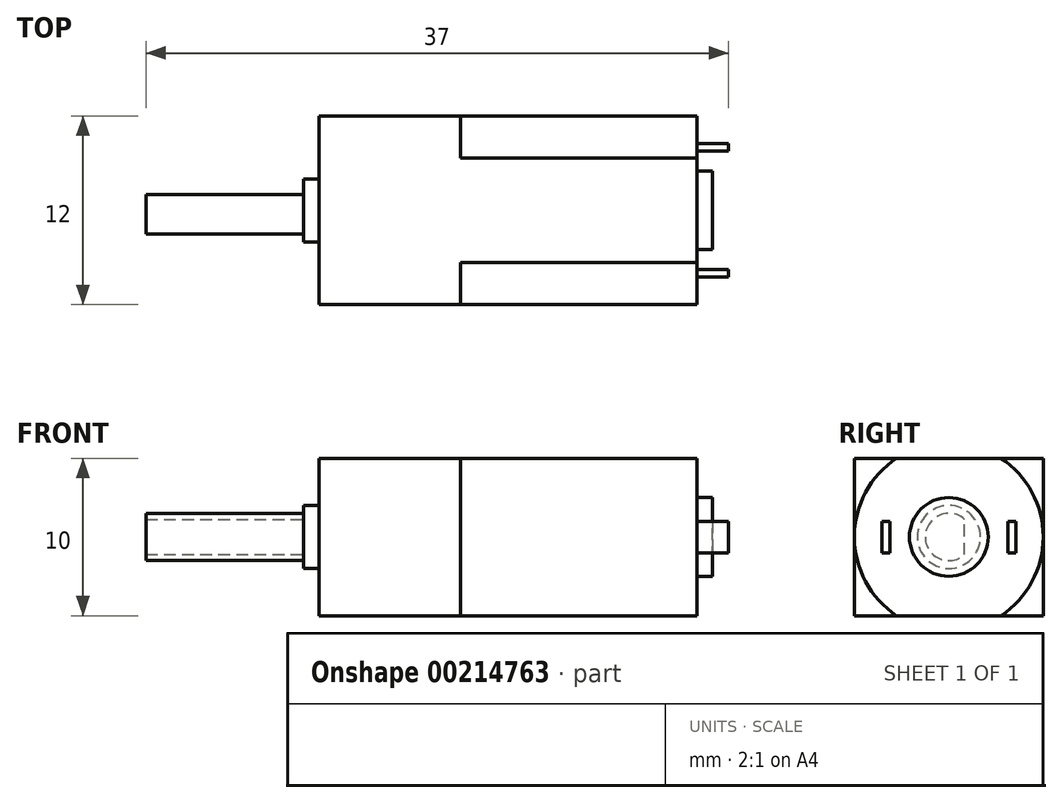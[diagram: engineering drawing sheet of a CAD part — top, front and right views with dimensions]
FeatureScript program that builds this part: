
annotation { "Feature Type Name" : "Feature", "Feature Type Description" : "" }
export const myFeature = defineFeature(function(context is Context, id is Id, definition is map)
    precondition{}
    {
        {
            var Q0;
            Q0=qCreatedBy(makeId("Right.planeOp"),FACE);
            var sketch = newSketch(context, id + "F0", { "sketchPlane" : qUnion([Q0])});
            skLineSegment(sketch, "E0.bottom", {"start": v(6, -5) * mm, "end": v(-6, -5) * mm});
            skLineSegment(sketch, "E0.top", {"start": v(6, 5) * mm, "end": v(-6, 5) * mm});
            skLineSegment(sketch, "E0.left", {"start": v(6, -5) * mm, "end": v(6, 5) * mm});
            skLineSegment(sketch, "E0.right", {"start": v(-6, -5) * mm, "end": v(-6, 5) * mm});
            skPoint(sketch, "E0.middle", {"position": v(0, 0) * mm});
            skCircle(sketch, "E1", {"center": v(0, 0) * mm, "radius": 2 * mm});
            skSolve(sketch);
        }
        {
            var Q0;
            Q0=makeQuery(id+"F0.imprint","IMPRINT",FACE,{"disambiguationData":[TD([[makeQuery(id+"F0.imprint","IMPRINT",EDGE,{"derivedFrom":sQuery(id+"F0.wireOp",EDGE,"E0.bottom")}),-1.0]])]});
            var Q1;
            Q1=makeQuery(id+"F0.imprint","IMPRINT",FACE,{"disambiguationData":[TD([[makeQuery(id+"F0.imprint","IMPRINT",EDGE,{"derivedFrom":sQuery(id+"F0.wireOp",EDGE,"E1")}),1.0]])]});
            extrude(context, id + "F1", {"entities" : qUnion([Q0, Q1]), "depth" : 9 * mm});
        }
        {
            var Q0;
            Q0=makeQuery(id+"F0.imprint","IMPRINT",FACE,{"disambiguationData":[TD([[makeQuery(id+"F0.imprint","IMPRINT",EDGE,{"derivedFrom":sQuery(id+"F0.wireOp",EDGE,"E1")}),1.0]])]});
            extrude(context, id + "F2", {"entities" : qUnion([Q0]), "operationType" : NewBodyOperationType.ADD, "oppositeDirection" : true, "depth" : 1 * mm});
        }
        {
            var Q0;
            Q0=makeQuery(id+"F2.opExtrude","CAP_FACE",FACE,{"disambiguationData":[OSD([sQuery(id+"F0.wireOp",EDGE,"E1")])],"isStart":false});
            var sketch = newSketch(context, id + "F3", { "sketchPlane" : qUnion([Q0])});
            skCircle(sketch, "E2", {"center": v(0, 0) * mm, "radius": 1.5 * mm});
            skLineSegment(sketch, "E3", {"start": v(-1, -1.12) * mm, "end": v(-1, 1.12) * mm});
            skSolve(sketch);
        }
        {
            var Q0;
            {var subQ0=sQuery(id+"F3.wireOp",EDGE,"E3");Q0=makeQuery(id+"F3.imprint","IMPRINT",FACE,{"disambiguationData":[TD([[makeQuery(id+"F3.imprint","IMPRINT",EDGE,{"derivedFrom":subQ0}),-1.0]])]});}
            extrude(context, id + "F4", {"entities" : qUnion([Q0]), "operationType" : NewBodyOperationType.ADD, "depth" : 10 * mm});
        }
        {
            var Q0;
            Q0=makeQuery(id+"F1.opExtrude","CAP_FACE",FACE,{"disambiguationData":[OSD([sQuery(id+"F0.wireOp",EDGE,"E0.bottom"),sQuery(id+"F0.wireOp",EDGE,"E0.top"),sQuery(id+"F0.wireOp",EDGE,"E0.left"),sQuery(id+"F0.wireOp",EDGE,"E0.right")])],"isStart":false});
            var sketch = newSketch(context, id + "F5", { "sketchPlane" : qUnion([Q0])});
            skArc(sketch, "E4", {"start": v(-3.32, 5) * mm, "mid": v(-6, 0) * mm, "end": v(-3.32, -5) * mm});
            skLineSegment(sketch, "E5.0", {"start": v(6, 5) * mm, "end": v(-6, 5) * mm});
            skLineSegment(sketch, "E6.0", {"start": v(6, -5) * mm, "end": v(-6, -5) * mm});
            skArc(sketch, "E7.trimOffspring", {"start": v(3.32, -5) * mm, "mid": v(6, 0) * mm, "end": v(3.32, 5) * mm});
            skSolve(sketch);
        }
        {
            var Q0;
            {var subQ1=sQuery(id+"F5.wireOp",EDGE,"E4");var subQ5=sQuery(id+"F5.wireOp",EDGE,"E5.0");var subQ6=makeQuery(id+"F5.imprint","INTERSECT",VERTEX,{"derivedFrom":[subQ1,subQ5]});Q0=makeQuery(id+"F5.imprint","IMPRINT",FACE,{"disambiguationData":[TD([[makeQuery(id+"F5.imprint","IMPRINT",EDGE,{"disambiguationData":[TD([[subQ6,-1.0]])],"derivedFrom":subQ1}),1.0]])]});}
            extrude(context, id + "F6", {"entities" : qUnion([Q0]), "operationType" : NewBodyOperationType.ADD, "depth" : 15 * mm});
        }
        {
            var Q0;
            Q0=makeQuery(id+"F6.opExtrude","CAP_FACE",FACE,{"disambiguationData":[OSD([sQuery(id+"F5.wireOp",EDGE,"E4"),sQuery(id+"F5.wireOp",EDGE,"E5.0"),sQuery(id+"F5.wireOp",EDGE,"E6.0"),sQuery(id+"F5.wireOp",EDGE,"E7.trimOffspring")])],"isStart":false});
            var sketch = newSketch(context, id + "F7", { "sketchPlane" : qUnion([Q0])});
            skCircle(sketch, "E8", {"center": v(0, 0) * mm, "radius": 2.5 * mm});
            skLineSegment(sketch, "E9.bottom", {"start": v(3.75, -1) * mm, "end": v(4.25, -1) * mm});
            skLineSegment(sketch, "E9.top", {"start": v(3.75, 1) * mm, "end": v(4.25, 1) * mm});
            skLineSegment(sketch, "E9.left", {"start": v(3.75, -1) * mm, "end": v(3.75, 1) * mm});
            skLineSegment(sketch, "E9.right", {"start": v(4.25, -1) * mm, "end": v(4.25, 1) * mm});
            skPoint(sketch, "E9.middle", {"position": v(4, 0) * mm});
            skLineSegment(sketch, "E10.bottom", {"start": v(-3.75, -1) * mm, "end": v(-4.25, -1) * mm});
            skLineSegment(sketch, "E10.top", {"start": v(-3.75, 1) * mm, "end": v(-4.25, 1) * mm});
            skLineSegment(sketch, "E10.left", {"start": v(-3.75, -1) * mm, "end": v(-3.75, 1) * mm});
            skLineSegment(sketch, "E10.right", {"start": v(-4.25, -1) * mm, "end": v(-4.25, 1) * mm});
            skPoint(sketch, "E10.middle", {"position": v(-4, 0) * mm});
            skSolve(sketch);
        }
        {
            var Q0;
            Q0=makeQuery(id+"F7.imprint","IMPRINT",FACE,{"disambiguationData":[TD([[makeQuery(id+"F7.imprint","IMPRINT",EDGE,{"derivedFrom":sQuery(id+"F7.wireOp",EDGE,"E8")}),1.0]])]});
            extrude(context, id + "F8", {"entities" : qUnion([Q0]), "operationType" : NewBodyOperationType.ADD, "depth" : 1 * mm});
        }
        {
            var Q0;
            Q0=makeQuery(id+"F7.imprint","IMPRINT",FACE,{"disambiguationData":[TD([[makeQuery(id+"F7.imprint","IMPRINT",EDGE,{"derivedFrom":sQuery(id+"F7.wireOp",EDGE,"E10.bottom")}),-1.0]])]});
            var Q1;
            Q1=makeQuery(id+"F7.imprint","IMPRINT",FACE,{"disambiguationData":[TD([[makeQuery(id+"F7.imprint","IMPRINT",EDGE,{"derivedFrom":sQuery(id+"F7.wireOp",EDGE,"E9.bottom")}),1.0]])]});
            extrude(context, id + "F9", {"entities" : qUnion([Q0, Q1]), "operationType" : NewBodyOperationType.ADD, "depth" : 2 * mm});
        }
    });
